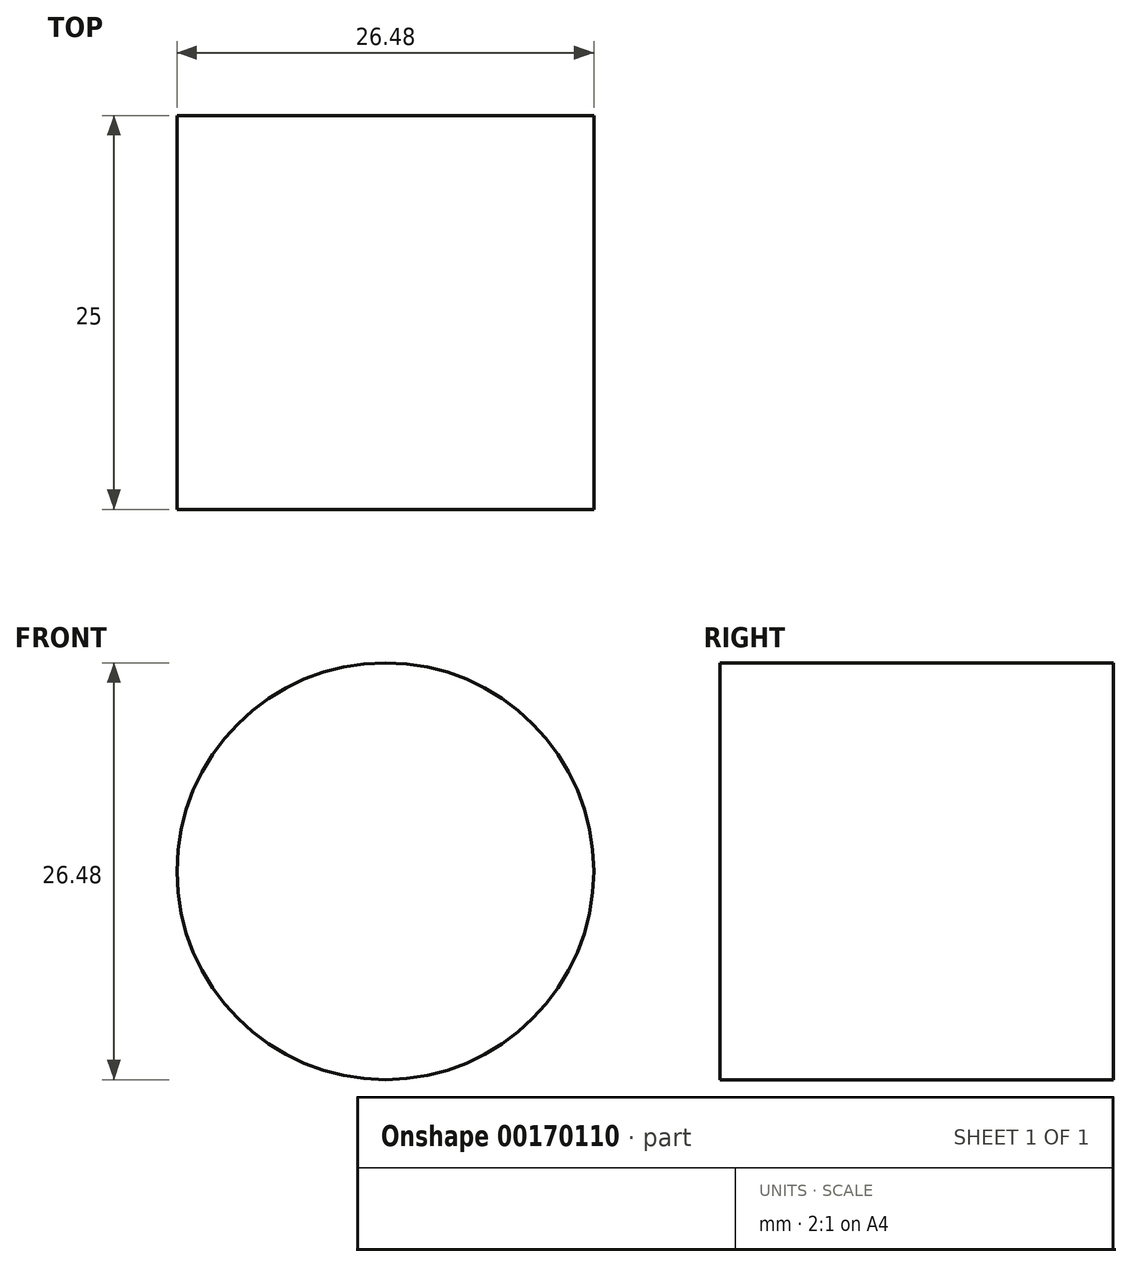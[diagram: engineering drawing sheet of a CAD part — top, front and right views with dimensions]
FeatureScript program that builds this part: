
annotation { "Feature Type Name" : "Feature", "Feature Type Description" : "" }
export const myFeature = defineFeature(function(context is Context, id is Id, definition is map)
    precondition{}
    {
        {
            var Q0;
            Q0=qCreatedBy(makeId("Front.planeOp"),FACE);
            var sketch = newSketch(context, id + "F0", { "sketchPlane" : qUnion([Q0])});
            skCircle(sketch, "E0", {"center": v(0, 0) * mm, "radius": 13.24 * mm});
            skSolve(sketch);
        }
        {
            var Q0;
            Q0=makeQuery(id+"F0.imprint","IMPRINT",FACE,{"disambiguationData":[TD([[makeQuery(id+"F0.imprint","IMPRINT",EDGE,{"derivedFrom":sQuery(id+"F0.wireOp",EDGE,"E0")}),1.0]])]});
            extrude(context, id + "F1", {"entities" : qUnion([Q0]), "depth" : 25 * mm});
        }
    });
